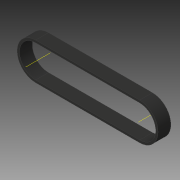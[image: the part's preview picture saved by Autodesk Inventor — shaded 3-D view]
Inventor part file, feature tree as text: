
AUTODESK INVENTOR PART (.ipt)
format: ipt  version: 2019 (Build 230136000, 136)  size: 156,160 bytes
history: native  units: in
note: dims shown in document units (in); Inventor stores cm internally (conversion verified against a paired STEP export)
features: sketch x4, extrude x1, other x1, projected_geometry x1
ambient origin geometry x8: Origin, YZ Plane, XZ Plane, XY Plane, X Axis, Y Axis, Z Axis, Center Point
bodies: Body1 (feature_tree)
feature tree (7):
  sketch  "Sketch1"  dims[d0=0.9023in d1=0.9023in]
  sketch  "Sketch2"  dims[d2=1.4174in]
  extrude  "Extrusion2"  Depth=0.9023in
  sketch  "Sketch5"  dims[d5=2.7165in d9=0.0787in d10=0.0598in d11=0.0299in d12=0.0219in d13=0.0219in d14=0.0059in d15=0.0059in d20=0.3346in d21=0.0in d22=0.0787in d23=0.0598in d24=0.0299in d25=0.0219in d26=0.0219in d27=0.0059in d28=0.0059in d29=0.0299in d30=0.0394in d31=0.0787in d32=0.0232in d34=0.0219in d35=0.0in d36=0.0in d37=0.0059in d38=0.0022in d39=0.0022in d40=0.0in d41=0.0in d42=0.0081in d43=0.0081in d44=0.0299in]
  other  "Work Axis1"
  sketch  "Sketch4"  dims[d3=1.4174in]
  projected_geometry  "Projected Loop1"
